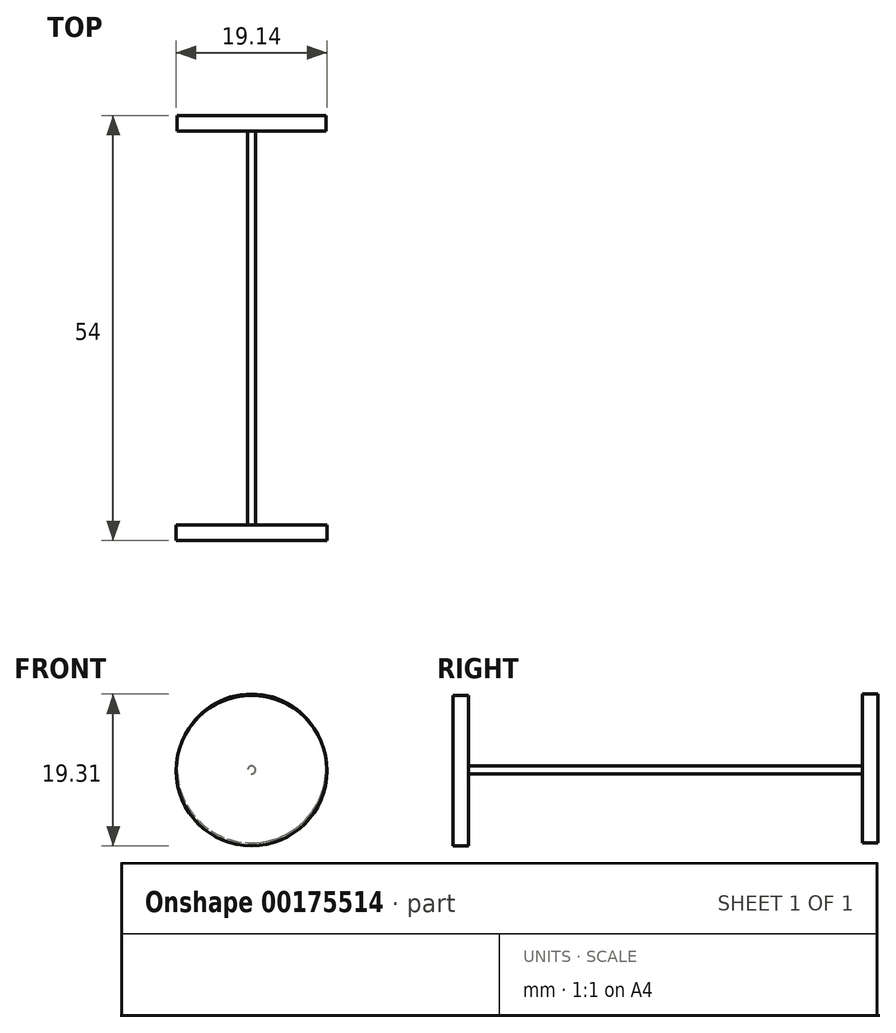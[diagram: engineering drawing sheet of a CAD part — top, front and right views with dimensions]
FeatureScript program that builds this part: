
annotation { "Feature Type Name" : "Feature", "Feature Type Description" : "" }
export const myFeature = defineFeature(function(context is Context, id is Id, definition is map)
    precondition{}
    {
        {
            var Q0;
            Q0=qCreatedBy(makeId("Front.planeOp"),FACE);
            var sketch = newSketch(context, id + "F0", { "sketchPlane" : qUnion([Q0])});
            skCircle(sketch, "E0", {"center": v(0, 8.7) * mm, "radius": 0.5 * mm});
            skSolve(sketch);
        }
        {
            var Q0;
            Q0=qSketchRegion(id+"F0",true);
            extrude(context, id + "F1", {"entities" : qUnion([Q0]), "depth" : 50 * mm});
        }
        {
            var Q0;
            Q0=qCreatedBy(makeId("Front.planeOp"),FACE);
            cPlane(context, id + "F2", {"entities" : qUnion([Q0]), "cplaneType" : CPlaneType.OFFSET, "offset" : 42 * mm, "width" : 150 * mm, "height" : 150 * mm});
        }
        {
            var Q0;
            Q0=qCreatedBy(makeId("Front.planeOp"),FACE);
            var sketch = newSketch(context, id + "F3", { "sketchPlane" : qUnion([Q0])});
            skCircle(sketch, "E1", {"center": v(0, 8.9) * mm, "radius": 9.46 * mm});
            skSolve(sketch);
        }
        {
            var Q0;
            Q0=qSketchRegion(id+"F3",true);
            extrude(context, id + "F4", {"entities" : qUnion([Q0]), "operationType" : NewBodyOperationType.ADD, "oppositeDirection" : true, "depth" : 2 * mm});
        }
        {
            var Q0;
            Q0=qCreatedBy(id+"F2.planeOp",FACE);
            cPlane(context, id + "F5", {"entities" : qUnion([Q0]), "cplaneType" : CPlaneType.OFFSET, "offset" : 8 * mm, "width" : 150 * mm, "height" : 150 * mm});
        }
        {
            var Q0;
            Q0=qCreatedBy(id+"F5.planeOp",FACE);
            var sketch = newSketch(context, id + "F6", { "sketchPlane" : qUnion([Q0])});
            skCircle(sketch, "E2", {"center": v(0, 8.63) * mm, "radius": 9.57 * mm});
            skSolve(sketch);
        }
        {
            var Q0;
            Q0=qSketchRegion(id+"F6",true);
            extrude(context, id + "F7", {"entities" : qUnion([Q0]), "operationType" : NewBodyOperationType.ADD, "depth" : 2 * mm});
        }
    });
